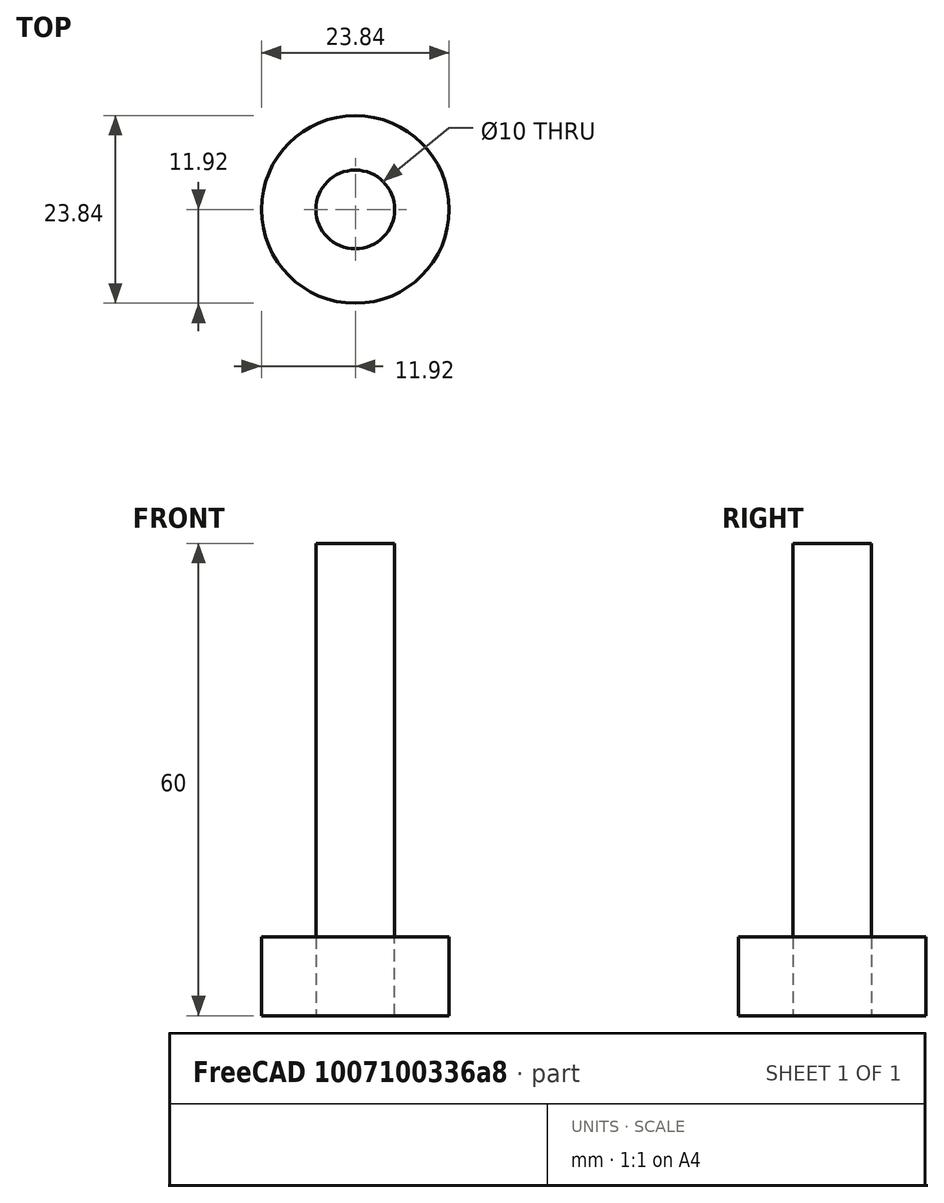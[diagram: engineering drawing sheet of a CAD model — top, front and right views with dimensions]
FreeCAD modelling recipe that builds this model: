
FCSTD DOCUMENT  (FreeCAD 1.1R20260414 (Git shallow))
Label: screw
License: All rights reserved
LicenseURL: https://en.wikipedia.org/wiki/All_rights_reserved
objects: App::Point×3, Sketcher::SketchObject×2, PartDesign::Pad×2, PartDesign::Body×2, App::Link×2, App::FeaturePython×2, Assembly::JointGroup×1, Assembly::AssemblyObject×1
note: 12 computed .brp shape members not serialized (recipe doc carries the construction recipe); baked Part::Feature solids carry a one-line shape summary decoded from their .brp

FEATURE [App::Point] Origin001
  Role = Origin
FEATURE [Sketcher::SketchObject] Sketch
  ArcFitTolerance = 1e-06
  AttachmentSupport = -> [Origin]
  ExternalTypes = [0]
  FullyConstrained = false
  MakeInternals = true
  MapMode = 5
  _ExternalGeoVersion = 1
  sketch-geometry (2):
    g0: Circle CenterX=0 CenterY=0 CenterZ=0 NormalX=0 NormalY=0 NormalZ=1 AngleXU=0 Radius=11.9213
    g1: Circle CenterX=0 CenterY=0 CenterZ=0 NormalX=0 NormalY=0 NormalZ=1 AngleXU=0 Radius=5
  constraints (3):
    c: Coincident(g0,g-1)
    c: Coincident(g1,g0)
    c: Diameter(g1) = 10
FEATURE [PartDesign::Pad] Pad
  Direction = (0,0,1)
  Length = 10
  Length2 = 10
  Profile = -> Sketch
  ReferenceAxis = -> Sketch [N_Axis]
  Refine = true
  SideType = 0
  Suppressed = false
  Type = 0
  Type2 = 0
FEATURE [PartDesign::Body] Body  label="nut"
  AllowCompound = true
  Group = -> [Sketch,Pad]
  Origin = -> Origin
  Tip = -> Pad
FEATURE [App::Point] Origin003
  Role = Origin
FEATURE [Sketcher::SketchObject] Sketch001
  ArcFitTolerance = 1e-06
  AttachmentSupport = -> [Origin002]
  ExternalTypes = [0]
  FullyConstrained = true
  MakeInternals = true
  MapMode = 5
  _ExternalGeoVersion = 1
  sketch-geometry (1):
    g0: Circle CenterX=0 CenterY=0 CenterZ=0 NormalX=0 NormalY=0 NormalZ=1 AngleXU=0 Radius=5
  constraints (2):
    c: Coincident(g0,g-1)
    c: Diameter(g0) = 10
FEATURE [PartDesign::Pad] Pad001
  Direction = (0,0,1)
  Length = 60
  Length2 = 10
  Profile = -> Sketch001
  ReferenceAxis = -> Sketch001 [N_Axis]
  Refine = true
  SideType = 0
  Suppressed = false
  Type = 0
  Type2 = 0
FEATURE [PartDesign::Body] Body001  label="screw"
  AllowCompound = true
  Group = -> [Sketch001,Pad001]
  Origin = -> Origin002
  Tip = -> Pad001
FEATURE [App::Point] Origin005  label="Origin006"
  Role = Origin
FEATURE [App::Link] screw  label="screw001"
  LinkedObject = -> Body001
FEATURE [App::FeaturePython] GroundedJoint  # Assembly grounded joint (typed FeaturePython)
  ObjectToGround = -> screw
FEATURE [App::Link] nut  label="nut001"
  LinkPlacement = pos=(0,0,18.4704) rot=(0,0,1;0.286472rad)
  LinkedObject = -> Body
  Placement = pos=(0,0,18.4704) rot=(0,0,1;0.286472rad)
FEATURE [App::FeaturePython] Joint  label="Cylindrical001"  # Assembly joint (typed FeaturePython)
  Angle = 0
  AngleMax = 0
  AngleMin = 0
  Detach1 = false
  Detach2 = false
  Distance = 0
  Distance2 = 0
  EnableAngleMax = false
  EnableAngleMin = false
  EnableLengthMax = false
  EnableLengthMin = false
  JointType = 2 (Cylindrical)
  LengthMax = 0
  LengthMin = 0
  Placement2 = pos=(0,0,30) rot=(0,0,1;0rad)
  Reference1 = -> nut [Pad.Edge5,Pad.Edge5]
  Reference2 = -> screw [Pad001.Face1,Pad001.Face1]
  Suppressed = false
FEATURE [Assembly::JointGroup] Joints
  Group = -> [GroundedJoint,Joint]
FEATURE [Assembly::AssemblyObject] Assembly
  Group = -> [Joints,screw,GroundedJoint,nut,Joint]
  Origin = -> Origin004
  Type = Assembly
